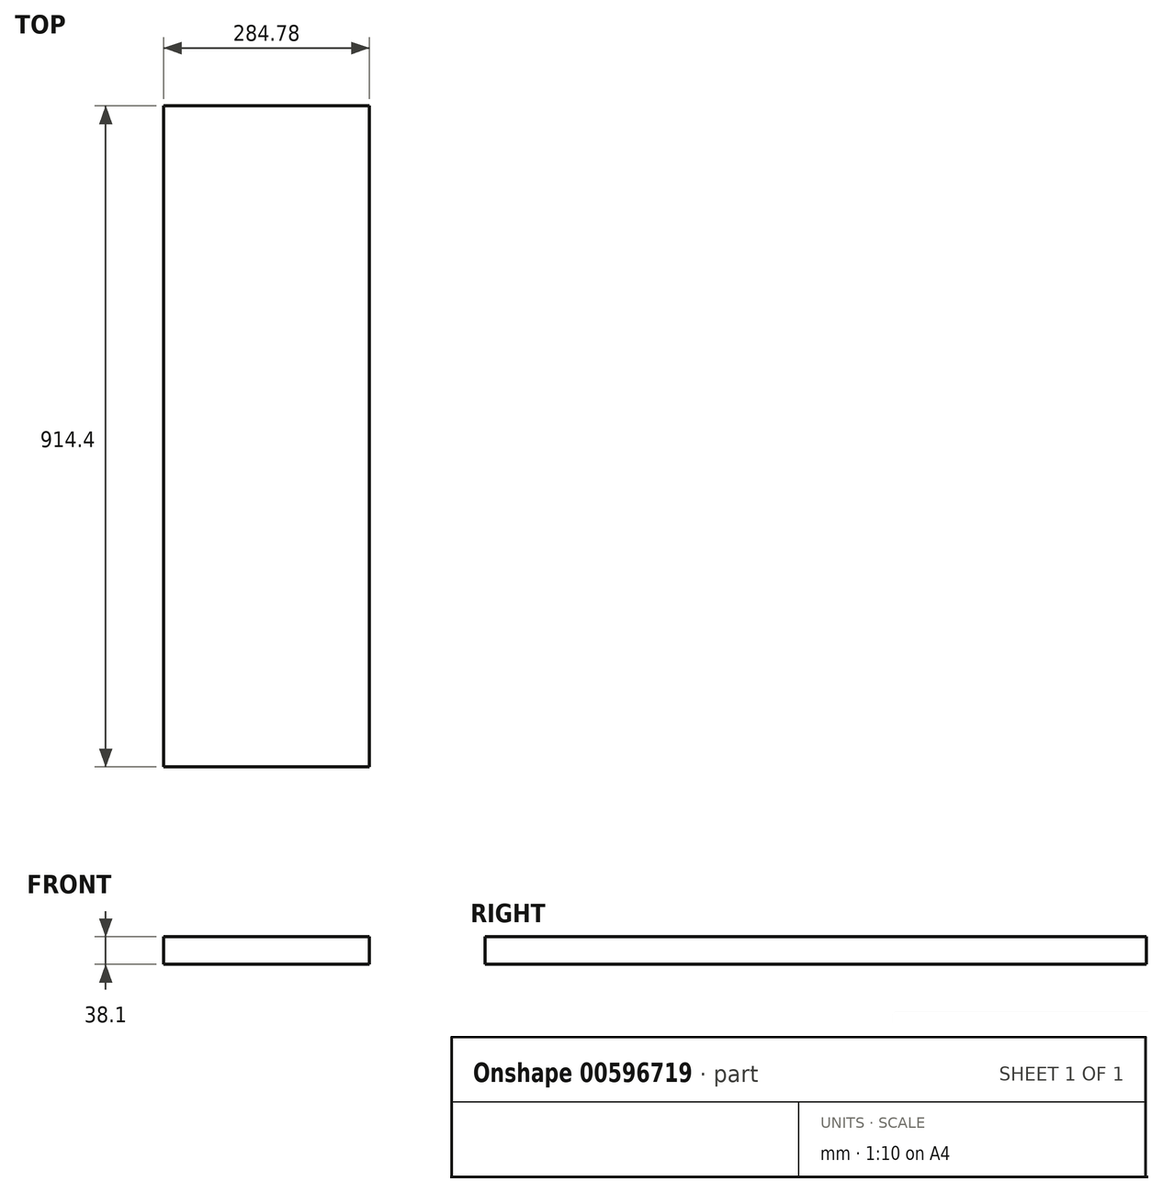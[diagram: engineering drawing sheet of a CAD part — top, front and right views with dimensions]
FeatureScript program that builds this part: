
annotation { "Feature Type Name" : "Feature", "Feature Type Description" : "" }
export const myFeature = defineFeature(function(context is Context, id is Id, definition is map)
    precondition{}
    {
        {
            var Q0;
            Q0=qCreatedBy(makeId("Top.planeOp"),FACE);
            var sketch = newSketch(context, id + "F0", { "sketchPlane" : qUnion([Q0])});
            skLineSegment(sketch, "E0.bottom", {"start": v(142.39, -457.2) * mm, "end": v(-142.39, -457.2) * mm});
            skLineSegment(sketch, "E0.top", {"start": v(142.39, 457.2) * mm, "end": v(-142.39, 457.2) * mm});
            skLineSegment(sketch, "E0.left", {"start": v(142.39, -457.2) * mm, "end": v(142.39, 457.2) * mm});
            skLineSegment(sketch, "E0.right", {"start": v(-142.39, -457.2) * mm, "end": v(-142.39, 457.2) * mm});
            skPoint(sketch, "E0.middle", {"position": v(0, 0) * mm});
            skSolve(sketch);
        }
        {
            var Q0;
            Q0 = qSketchRegion(id + "F0", true);
            extrude(context, id + "F1", {"entities" : qUnion([Q0]), "depth" : 38.1 * mm, "offsetDistance" : 25.4 * mm});
        }
    });
